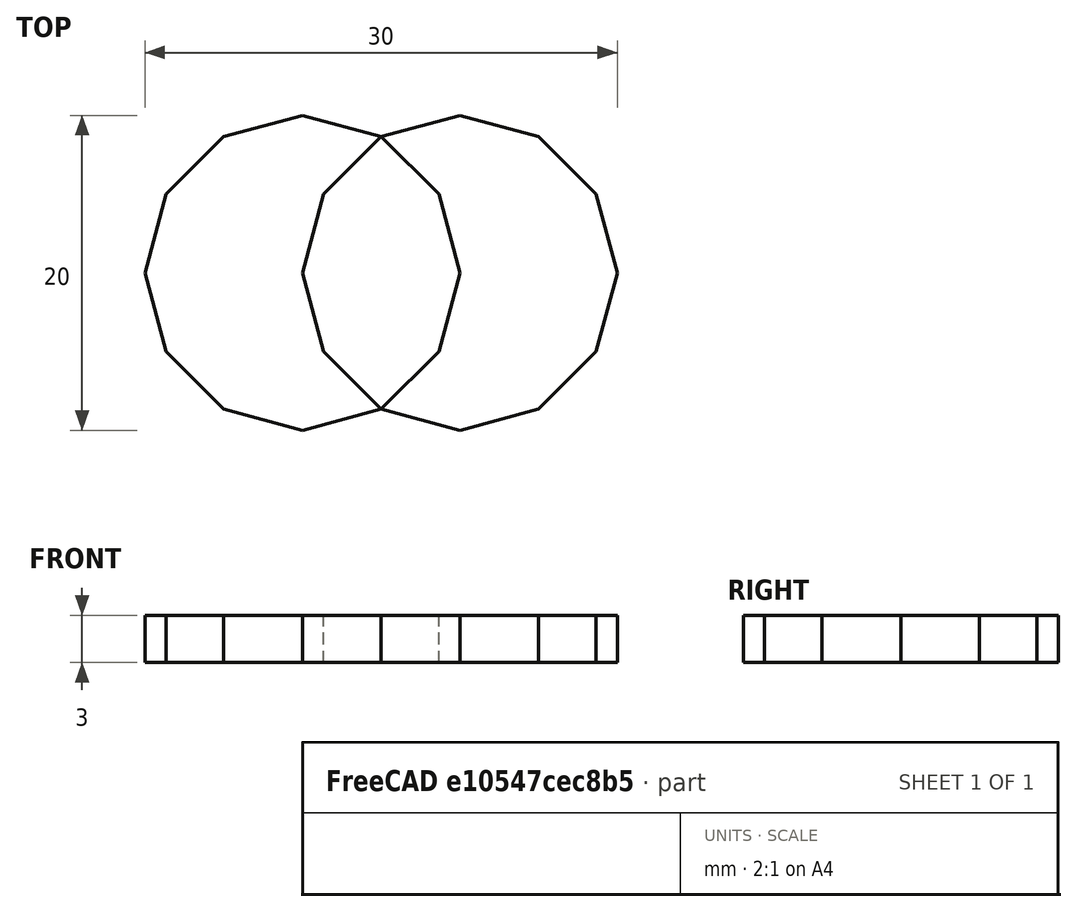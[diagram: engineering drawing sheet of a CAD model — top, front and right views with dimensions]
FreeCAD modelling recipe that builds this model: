
FCSTD DOCUMENT  (FreeCAD 0.21R33771 (Git))
Label: openscad_hull_testing
License: Creative Commons Attribution-ShareAlike 4.0
LicenseURL: https://creativecommons.org/licenses/by-sa/4.0/
objects: Part::Part2DObjectPython×2, Part::FeaturePython×2, Part::Fuse×1, Part::Extrusion×1
note: 6 computed .brp shape members not serialized (recipe doc carries the construction recipe); baked Part::Feature solids carry a one-line shape summary decoded from their .brp

FEATURE [Part::Part2DObjectPython] polygon  # Draft 2D object (typed FeaturePython)
  Area = 300
  ChamferSize = 0
  DrawMode = 0
  FacesNumber = 12
  FilletRadius = 0
  MakeFace = true
  Placement = pos=(10,0,0) rot=(0,0,1;0rad)
  Radius = 10
FEATURE [Part::Part2DObjectPython] polygon001  # Draft 2D object (typed FeaturePython)
  Area = 300
  ChamferSize = 0
  DrawMode = 0
  FacesNumber = 12
  FilletRadius = 0
  MakeFace = true
  Radius = 10
FEATURE [Part::Fuse] Linear_Extrude_Union
  Base = -> polygon
  Tool = -> polygon001
FEATURE [Part::FeaturePython] RefineLinearExtrude  # WARN: FeaturePython — macro-defined, semantics opaque (R4)
  Base = -> Linear_Extrude_Union
FEATURE [Part::Extrusion] LinearExtrude
  Base = -> RefineLinearExtrude
  Dir = (0,0,3)
  DirMode = 0
  FaceMakerClass = Part::FaceMakerBullseye
  LengthFwd = 0
  LengthRev = 0
  Solid = false
  Symmetric = false
FEATURE [Part::FeaturePython] hull  # WARN: FeaturePython — macro-defined, semantics opaque (R4)
  Arguments = []
  Children = -> [LinearExtrude]
  Operation = hull
